# Revit family: Reece_Cistern_Hideaway_Plus_Undercounter Cistern_Wall Hung
name_source: partatom
category: Plumbing Fixtures
revit_build: Autodesk Revit 2018 (Build: 20190510_1515(x64)
units: mm (PartAtom-declared; Revit-internal decimal feet)

## family parameters
Always vertical = Yes
Cut with Voids When Loaded = Yes
Part Type = Normal
Room Calculation Point = No
Round Connector Dimension = Use Diameter
Shared = No
Work Plane-Based = Yes

## types (1)
- White, Black and Blue
    Default Elevation = 0 mm  [stored 0 ft]
    Description = Hideaway+ Under Counter Cistern Wall Hung Frame (4 Star)
    Disclaimer = THIS FILE IS THE PROPERTY OF THE REECE GROUP. IT MAY NOT BE REPRODUCED, REVERSE-ENGINEERED OR MODIFIED. ANY REPUBLICATION, TRANSMISSION OR DISTRIBUTION FOR THE PURPOSE OF COMMERCIALLY EXPLOITING THE FILES IS PROHIBITED.
    Keynote = Product #9508061, Reece_Cistern_Hideaway_Plus_Undercounter Cistern_Wall Hung - White, Black and Blue
    Manufacturer = Hideaway
    Model = Plus
    Reece_Detail_Additional = Back to Wall
    Reece_Detail_Disclaimer = THIS FILE IS THE PROPERTY OF THE REECE GROUP. IT MAY NOT BE REPRODUCED, REVERSE-ENGINEERED OR MODIFIED. ANY REPUBLICATION, TRANSMISSION OR DISTRIBUTION FOR THE PURPOSE OF COMMERCIALLY EXPLOITING THE FILES IS PROHIBITED.
    Reece_Detail_Installation = Undercounter Cistern
    Reece_Material_Cistern = Reece_Acrylic_White
    Reece_Material_Colour = Reece_Plastic_Black
    Reece_Material_Main = Reece_Metal_Steel Enamelled_Blue
    Reece_Material_Secondary = Reece_Brass_Brushed Stainless Steel
    Reece_Overall_Width = 500 mm
    Reece_Product_Brand = Hideaway
    Reece_Product_Description = Hideaway+ Under Counter Cistern Wall Hung Frame (4 Star)
    Reece_Product_Number = 9508061
    Reece_Product_Sub Brand = Plus
    Reece_Product_Type = Cistern
    Reece_Product_Web Page = https://www.reece.com.au
    Reece_Water_Supply_Connection = 12 mm  [stored 0.0393701 ft]
    Type Comments = Cistern
    URL = https://www.reece.com.au

note: [stored X ft] marks values corroborated as IEEE doubles in the binary element streams (Revit-internal decimal feet)

## geometry (parser evidence)
native form markers: Sweep x7
no freeform markers — native parametric forms only
